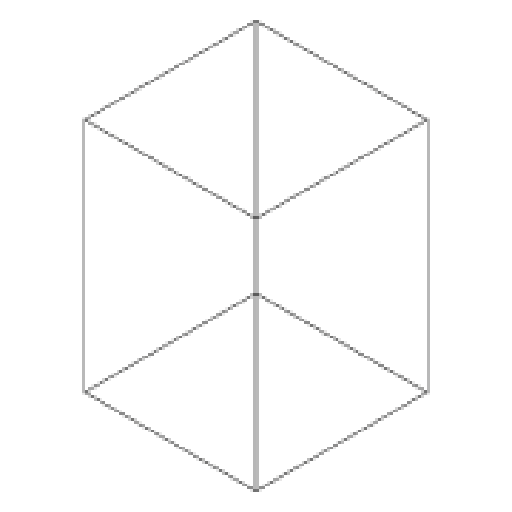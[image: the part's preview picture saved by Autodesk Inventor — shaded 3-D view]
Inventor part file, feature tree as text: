
AUTODESK INVENTOR PART (.ipt)
format: ipt  version: 2023 (Build 270158000, 158)  size: 153,088 bytes
history: native  units: in
note: dims shown in document units (in); Inventor stores cm internally (conversion verified against a paired STEP export)
features: extrude x4, sketch x4, projected_geometry x3, fillet x1
ambient origin geometry x8: Origin, YZ Plane, XZ Plane, XY Plane, X Axis, Y Axis, Z Axis, Center Point
bodies: Solid1 (feature_tree)
feature tree (12):
  extrude  "Extrusion1"  Depth=78.7402in TaperAngle=0.0deg
  extrude  "Extrusion2"  TaperAngle=0.0deg  [1 undecoded]
  extrude  "Extrusion3"  TaperAngle=0.0deg  [1 undecoded]
  extrude  "Extrusion4"  TaperAngle=0.0deg  [1 undecoded]
  fillet  "Fillet1"  Radius=0.25in
  sketch  "Sketch1"  dims[d0=78.7402in d2=78.7402in d3=0.0in]
  sketch  "Sketch2"  dims[d4=0.5in d5=0.0in d6=0.0in]
  projected_geometry  "Projected Loop1"
  sketch  "Sketch3"  dims[d7=0.5in d8=0.0in d9=0.0in]
  projected_geometry  "Projected Loop2"
  sketch  "Sketch4"  dims[d10=0.5in d11=0.0in d12=0.0in d13=0.25in]
  projected_geometry  "Projected Loop3"
note: 3 required parameter values undecoded (feature->parameter linkage not recoverable at this tier; creation-order binding heuristic only, values carry confidence <= 0.55)
